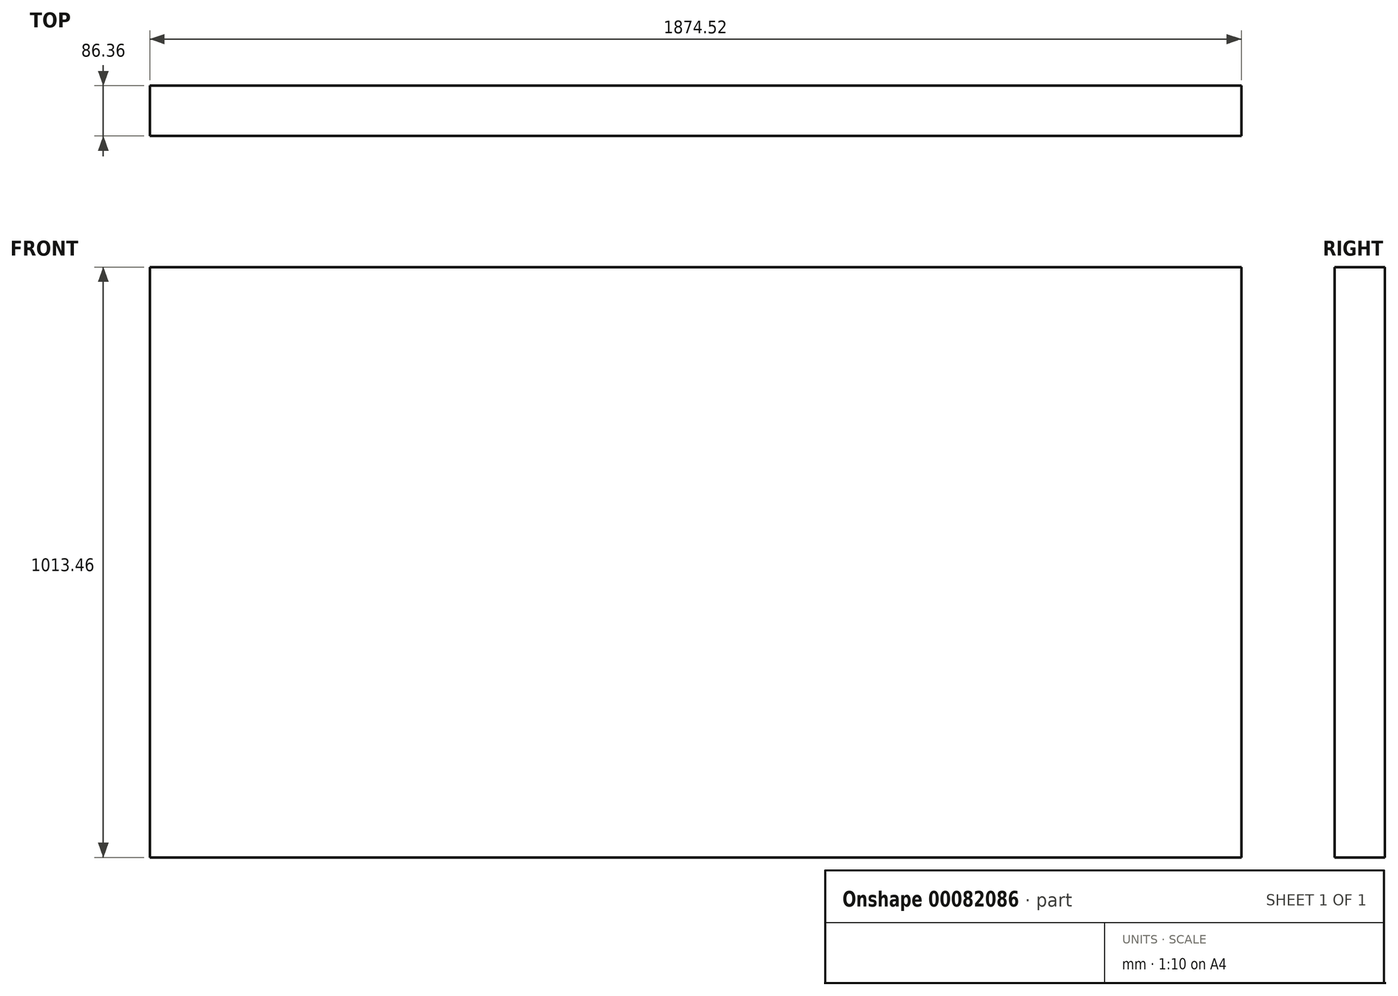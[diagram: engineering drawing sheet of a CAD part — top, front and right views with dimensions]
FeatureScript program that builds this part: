
annotation { "Feature Type Name" : "Feature", "Feature Type Description" : "" }
export const myFeature = defineFeature(function(context is Context, id is Id, definition is map)
    precondition{}
    {
        {
            var Q0;
            Q0=qCreatedBy(makeId("Front.planeOp"),FACE);
            var sketch = newSketch(context, id + "F0", { "sketchPlane" : qUnion([Q0])});
            skLineSegment(sketch, "E0.bottom", {"start": v(0, 0) * mm, "end": v(-1874.52, 0) * mm});
            skLineSegment(sketch, "E0.top", {"start": v(0, 1013.46) * mm, "end": v(-1874.52, 1013.46) * mm});
            skLineSegment(sketch, "E0.left", {"start": v(0, 0) * mm, "end": v(0, 1013.46) * mm});
            skLineSegment(sketch, "E0.right", {"start": v(-1874.52, 0) * mm, "end": v(-1874.52, 1013.46) * mm});
            skSolve(sketch);
        }
        {
            var Q0;
            Q0=makeQuery(id+"F0.imprint","IMPRINT",FACE,{"disambiguationData":[TD([[makeQuery(id+"F0.imprint","IMPRINT",EDGE,{"derivedFrom":sQuery(id+"F0.wireOp",EDGE,"E0.bottom")}),-1.0]])]});
            extrude(context, id + "F1", {"entities" : qUnion([Q0]), "depth" : 86.36 * mm});
        }
    });
